# Revit family: Aluco Skylight AIR (pl)
name_source: partatom
category: Modele ogólne
units: mm (PartAtom-declared; Revit-internal decimal feet)

## family parameters
Może być obiektem nadrzędnym dla zbrojenia = Nie
Numer OmniClass = 23.60.70.14.11
Oparty na płaszczyźnie roboczej = Tak
Punkt obliczania pomieszczeń = Nie
Tnij formami wycięć po wczytaniu = Tak
Typ części = Normalny
Tytuł OmniClass = Smoke Dampers
Współdzielony = Nie
Wymiar okrągłego złącza = Użyj średnicy
Zawsze pionowo = Nie

## types (2) — shared parameters
IfcExportAs = "IfcWindowType"
Klasa bezpieczeństwa pożarowego = BRoof (t1)
Klasa bezpieczeństwa przed upadkiem z wysokości = SB 1200
Komentarze do typu = Klapa wentylacyjna
Materiał profili = Aluco - aluminium
Materiał płyt = Aluco - poliwęglan
Model = Skylight AIR
Obraz typu = ALUCO SKYLIGHT AIR.png
Odporność na obciążenie dociskające = DL 2500
Odporność na obciążenie odrywające = UL 1500
Opis = Klapy do wentylacji codziennej dedykowane do świetlików łukowych
Producent = ALUCO SYSTEM SP. Z O.O
URL = https://aluco.com.pl
URL produktu = https://aluco.com.pl
zero-valued in all types: Domyślna rzędna

## per-type parameters (varying)
| type | Rodzaj napędu | Zasilanie |
| z napędem elektrycznym | napęd elektryczny | 230 V |
| z napędem mechanicznym | napęd mechaniczny | 0 V |
